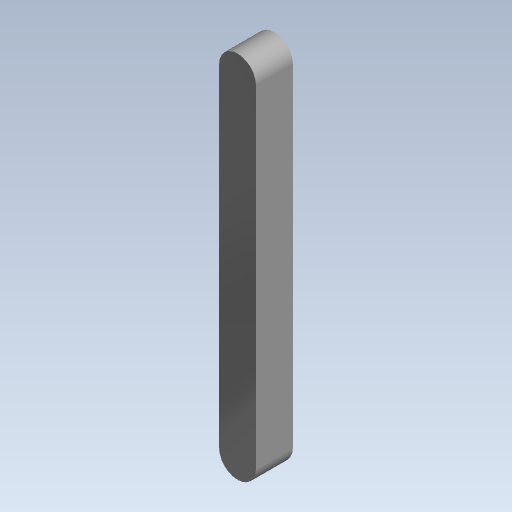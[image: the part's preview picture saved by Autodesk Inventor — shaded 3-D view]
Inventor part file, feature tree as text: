
AUTODESK INVENTOR PART (.ipt)
format: ipt  version: 2020 (Build 240168000, 168)  size: 60,416 bytes
history: native  units: mm (DEFAULTED — no unit token found)
features: fillet x1
ambient origin geometry x8: Origin, YZ Plane, XZ Plane, XY Plane, X Axis, Y Axis, Z Axis, Center Point
bodies: Solid1 (feature_tree)
feature tree (1):
  fillet  "Fillet1"  [1 undecoded]
note: 1 required parameter value undecoded (feature->parameter linkage not recoverable at this tier; creation-order binding heuristic only, values carry confidence <= 0.55)
